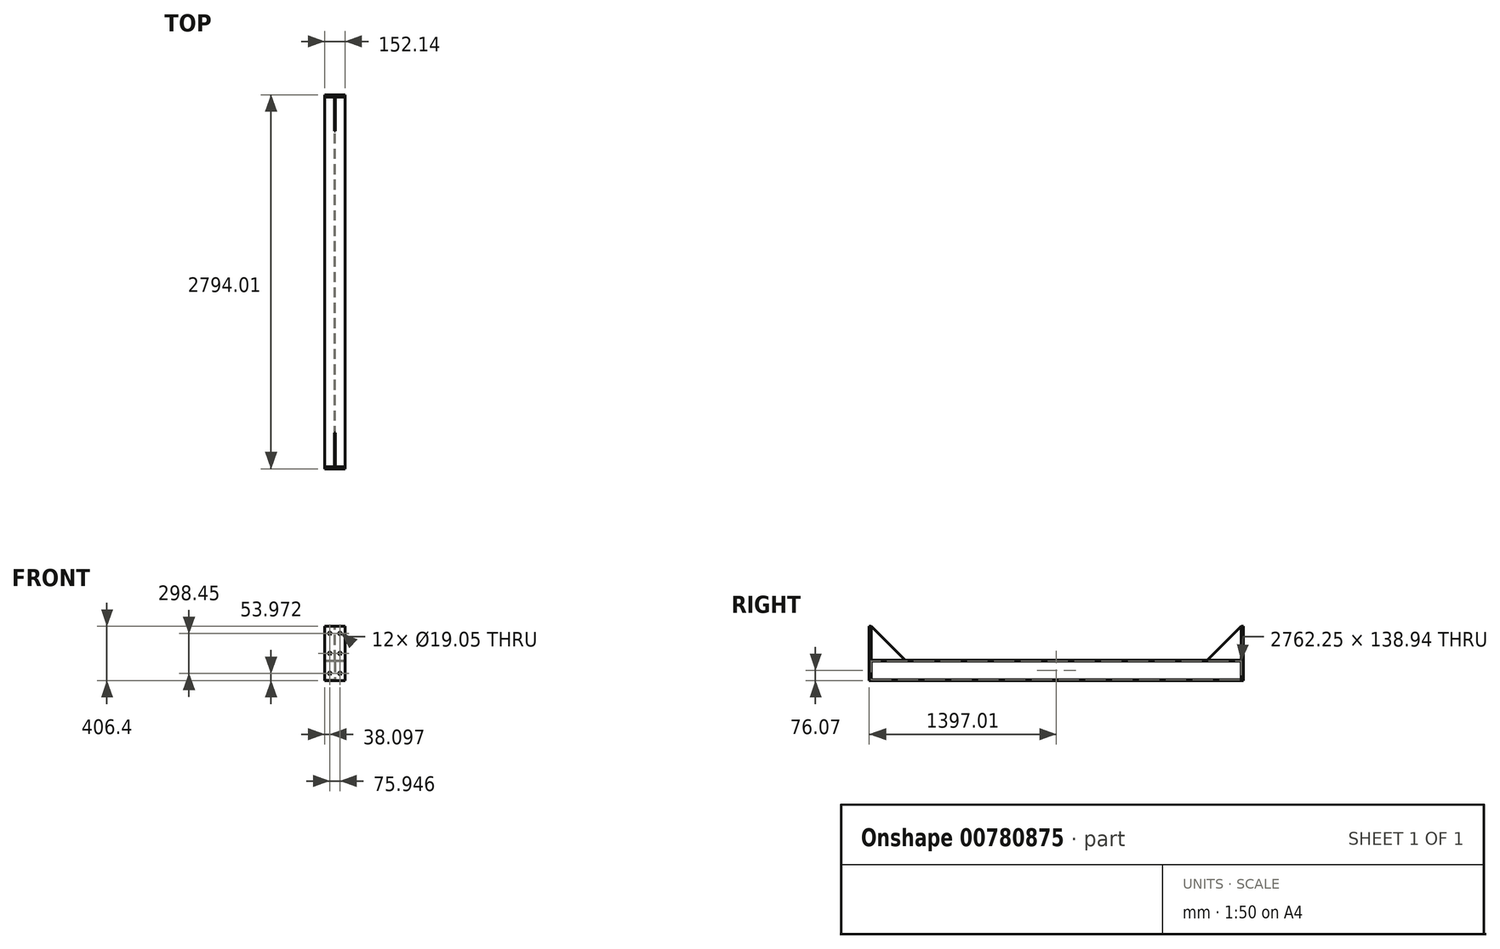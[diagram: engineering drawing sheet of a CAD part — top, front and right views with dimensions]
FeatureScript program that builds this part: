
annotation { "Feature Type Name" : "Feature", "Feature Type Description" : "" }
export const myFeature = defineFeature(function(context is Context, id is Id, definition is map)
    precondition{}
    {
        {
            var Q0;
            Q0=qCreatedBy(makeId("Front.planeOp"),FACE);
            var sketch = newSketch(context, id + "F0", { "sketchPlane" : qUnion([Q0])});
            skLineSegment(sketch, "E0", {"start": v(0, -76.07) * mm, "end": v(0, 76.07) * mm, "construction": true});
            skLineSegment(sketch, "E1", {"start": v(-76.07, 76.07) * mm, "end": v(76.07, 76.07) * mm});
            skLineSegment(sketch, "E2", {"start": v(-76.07, -76.07) * mm, "end": v(76.07, -76.07) * mm});
            skLineSegment(sketch, "E3", {"start": v(-76.07, 76.07) * mm, "end": v(-76.07, 69.47) * mm});
            skLineSegment(sketch, "E4", {"start": v(-76.07, 69.47) * mm, "end": v(-9.27, 69.47) * mm});
            skLineSegment(sketch, "E5", {"start": v(-2.92, 63.12) * mm, "end": v(-2.92, -63.12) * mm});
            skLineSegment(sketch, "E6", {"start": v(-9.27, -69.47) * mm, "end": v(-76.07, -69.47) * mm});
            skLineSegment(sketch, "E7", {"start": v(-76.07, -69.47) * mm, "end": v(-76.07, -76.07) * mm});
            skLineSegment(sketch, "E8", {"start": v(-2.92, 69.47) * mm, "end": v(2.92, 69.47) * mm, "construction": true});
            skLineSegment(sketch, "E9", {"start": v(9.27, 69.47) * mm, "end": v(76.07, 69.47) * mm});
            skLineSegment(sketch, "E10", {"start": v(76.07, 69.47) * mm, "end": v(76.07, 76.07) * mm});
            skLineSegment(sketch, "E11", {"start": v(-2.92, -69.47) * mm, "end": v(2.92, -69.47) * mm, "construction": true});
            skLineSegment(sketch, "E12", {"start": v(2.92, 63.12) * mm, "end": v(2.92, -63.12) * mm});
            skLineSegment(sketch, "E13", {"start": v(9.27, -69.47) * mm, "end": v(76.07, -69.47) * mm});
            skLineSegment(sketch, "E14", {"start": v(76.07, -69.47) * mm, "end": v(76.07, -76.07) * mm});
            skLineSegment(sketch, "E15", {"start": v(0, 69.47) * mm, "end": v(0, -69.47) * mm, "construction": true});
            skPoint(sketch, "E16.visualSharp", {"position": v(2.92, 69.47) * mm});
            skArc(sketch, "E16.filletArc", {"start": v(9.27, 69.47) * mm, "mid": v(4.78, 67.6) * mm, "end": v(2.92, 63.12) * mm});
            skPoint(sketch, "E17.visualSharp", {"position": v(-2.92, 69.47) * mm});
            skArc(sketch, "E17.filletArc", {"start": v(-2.92, 63.12) * mm, "mid": v(-4.78, 67.6) * mm, "end": v(-9.27, 69.47) * mm});
            skPoint(sketch, "E18.visualSharp", {"position": v(-2.92, -69.47) * mm});
            skArc(sketch, "E18.filletArc", {"start": v(-9.27, -69.47) * mm, "mid": v(-4.78, -67.6) * mm, "end": v(-2.92, -63.12) * mm});
            skPoint(sketch, "E19.visualSharp", {"position": v(2.92, -69.47) * mm});
            skArc(sketch, "E19.filletArc", {"start": v(2.92, -63.12) * mm, "mid": v(4.78, -67.6) * mm, "end": v(9.27, -69.47) * mm});
            skSolve(sketch);
        }
        {
            var Q0;
            Q0=makeQuery(id+"F0.imprint","IMPRINT",FACE,{"disambiguationData":[TD([[makeQuery(id+"F0.imprint","IMPRINT",EDGE,{"derivedFrom":sQuery(id+"F0.wireOp",EDGE,"E1")}),-1.0]])]});
            extrude(context, id + "F1", {"entities" : qUnion([Q0]), "depth" : 2762.25 * mm, "offsetDistance" : 25.4 * mm});
        }
        {
            var Q0;
            Q0=makeQuery(id+"F1.opExtrude","CAP_FACE",FACE,{"disambiguationData":[OSD([sQuery(id+"F0.wireOp",EDGE,"E1"),sQuery(id+"F0.wireOp",EDGE,"E2"),sQuery(id+"F0.wireOp",EDGE,"E3"),sQuery(id+"F0.wireOp",EDGE,"E4"),sQuery(id+"F0.wireOp",EDGE,"E5"),sQuery(id+"F0.wireOp",EDGE,"E6"),sQuery(id+"F0.wireOp",EDGE,"E7"),sQuery(id+"F0.wireOp",EDGE,"E9"),sQuery(id+"F0.wireOp",EDGE,"E10"),sQuery(id+"F0.wireOp",EDGE,"E12"),sQuery(id+"F0.wireOp",EDGE,"E13"),sQuery(id+"F0.wireOp",EDGE,"E14"),sQuery(id+"F0.wireOp",EDGE,"E16.filletArc"),sQuery(id+"F0.wireOp",EDGE,"E17.filletArc"),sQuery(id+"F0.wireOp",EDGE,"E18.filletArc"),sQuery(id+"F0.wireOp",EDGE,"E19.filletArc")])],"isStart":false});
            var sketch = newSketch(context, id + "F2", { "sketchPlane" : qUnion([Q0])});
            skLineSegment(sketch, "E20.0", {"start": v(-76.07, -76.07) * mm, "end": v(76.07, -76.07) * mm});
            skLineSegment(sketch, "E21", {"start": v(-76.07, -76.07) * mm, "end": v(-76.07, 330.33) * mm});
            skLineSegment(sketch, "E22", {"start": v(76.07, -76.07) * mm, "end": v(76.07, 330.33) * mm});
            skLineSegment(sketch, "E23", {"start": v(76.07, 330.33) * mm, "end": v(-76.07, 330.33) * mm});
            skSolve(sketch);
        }
        {
            var Q0;
            {var subQ2=makeQuery(id+"F1.opExtrude","CAP_EDGE",EDGE,{"disambiguationData":[OSD([sQuery(id+"F0.wireOp",EDGE,"E9")])],"isStart":false});Q0=makeQuery(id+"F2.imprint","IMPRINT",FACE,{"disambiguationData":[TD([[makeQuery(id+"F2.imprint","IMPRINT",EDGE,{"derivedFrom":subQ2}),-1.0]])]});}
            var Q1;
            {var subQ2=makeQuery(id+"F1.opExtrude","CAP_EDGE",EDGE,{"disambiguationData":[OSD([sQuery(id+"F0.wireOp",EDGE,"E4")])],"isStart":false});Q1=makeQuery(id+"F2.imprint","IMPRINT",FACE,{"disambiguationData":[TD([[makeQuery(id+"F2.imprint","IMPRINT",EDGE,{"derivedFrom":subQ2}),-1.0]])]});}
            var Q2;
            {var subQ2=sQuery(id+"F2.wireOp",EDGE,"E23");Q2=makeQuery(id+"F2.imprint","IMPRINT",FACE,{"disambiguationData":[TD([[makeQuery(id+"F2.imprint","IMPRINT",EDGE,{"derivedFrom":subQ2}),1.0]])]});}
            var Q3;
            {var subQ4=sQuery(id+"F2.wireOp",EDGE,"E20.0");Q3=makeQuery(id+"F2.imprint","IMPRINT",FACE,{"disambiguationData":[TD([[makeQuery(id+"F2.imprint","IMPRINT",EDGE,{"derivedFrom":subQ4}),1.0]])]});}
            extrude(context, id + "F3", {"entities" : qUnion([Q0, Q1, Q2, Q3]), "operationType" : NewBodyOperationType.ADD, "depth" : 15.88 * mm, "offsetDistance" : 25.4 * mm});
        }
        {
            var Q0;
            Q0=makeQuery(id+"F1.opExtrude","CAP_FACE",FACE,{"disambiguationData":[OSD([sQuery(id+"F0.wireOp",EDGE,"E1"),sQuery(id+"F0.wireOp",EDGE,"E2"),sQuery(id+"F0.wireOp",EDGE,"E3"),sQuery(id+"F0.wireOp",EDGE,"E4"),sQuery(id+"F0.wireOp",EDGE,"E5"),sQuery(id+"F0.wireOp",EDGE,"E6"),sQuery(id+"F0.wireOp",EDGE,"E7"),sQuery(id+"F0.wireOp",EDGE,"E9"),sQuery(id+"F0.wireOp",EDGE,"E10"),sQuery(id+"F0.wireOp",EDGE,"E12"),sQuery(id+"F0.wireOp",EDGE,"E13"),sQuery(id+"F0.wireOp",EDGE,"E14"),sQuery(id+"F0.wireOp",EDGE,"E16.filletArc"),sQuery(id+"F0.wireOp",EDGE,"E17.filletArc"),sQuery(id+"F0.wireOp",EDGE,"E18.filletArc"),sQuery(id+"F0.wireOp",EDGE,"E19.filletArc")])],"isStart":true});
            var sketch = newSketch(context, id + "F4", { "sketchPlane" : qUnion([Q0])});
            skLineSegment(sketch, "E24.0", {"start": v(76.07, -76.07) * mm, "end": v(-76.07, -76.07) * mm});
            skLineSegment(sketch, "E25", {"start": v(-76.07, -76.07) * mm, "end": v(-76.07, 330.33) * mm});
            skLineSegment(sketch, "E26", {"start": v(-76.07, 330.33) * mm, "end": v(76.07, 330.33) * mm});
            skLineSegment(sketch, "E27", {"start": v(76.07, 330.33) * mm, "end": v(76.07, -76.07) * mm});
            skSolve(sketch);
        }
        {
            var Q0;
            {var subQ2=sQuery(id+"F4.wireOp",EDGE,"E26");Q0=makeQuery(id+"F4.imprint","IMPRINT",FACE,{"disambiguationData":[TD([[makeQuery(id+"F4.imprint","IMPRINT",EDGE,{"derivedFrom":subQ2}),-1.0]])]});}
            var Q1;
            {var subQ3=sQuery(id+"F4.wireOp",EDGE,"E24.0");Q1=makeQuery(id+"F4.imprint","IMPRINT",FACE,{"disambiguationData":[TD([[makeQuery(id+"F4.imprint","IMPRINT",EDGE,{"derivedFrom":subQ3}),-1.0]])]});}
            var Q2;
            {var subQ1=makeQuery(id+"F1.opExtrude","CAP_EDGE",EDGE,{"disambiguationData":[OSD([sQuery(id+"F0.wireOp",EDGE,"E4")])],"isStart":true});Q2=makeQuery(id+"F4.imprint","IMPRINT",FACE,{"disambiguationData":[TD([[makeQuery(id+"F4.imprint","IMPRINT",EDGE,{"derivedFrom":subQ1}),1.0]])]});}
            var Q3;
            {var subQ0=makeQuery(id+"F1.opExtrude","CAP_EDGE",EDGE,{"disambiguationData":[OSD([sQuery(id+"F0.wireOp",EDGE,"E9")])],"isStart":true});Q3=makeQuery(id+"F4.imprint","IMPRINT",FACE,{"disambiguationData":[TD([[makeQuery(id+"F4.imprint","IMPRINT",EDGE,{"derivedFrom":subQ0}),1.0]])]});}
            extrude(context, id + "F5", {"entities" : qUnion([Q0, Q1, Q2, Q3]), "operationType" : NewBodyOperationType.ADD, "depth" : 15.88 * mm, "offsetDistance" : 25.4 * mm});
        }
        {
            var Q0;
            Q0=qCreatedBy(makeId("Right.planeOp"),FACE);
            var sketch = newSketch(context, id + "F6", { "sketchPlane" : qUnion([Q0])});
            skLineSegment(sketch, "E28.0", {"start": v(0, 330.07) * mm, "end": v(0, 76.07) * mm});
            skLineSegment(sketch, "E29", {"start": v(0, 76.07) * mm, "end": v(-254, 76.07) * mm});
            skLineSegment(sketch, "E30", {"start": v(-254, 76.07) * mm, "end": v(0, 330.07) * mm});
            skPoint(sketch, "E31.orphan", {"position": v(0, 330.33) * mm});
            skLineSegment(sketch, "E32.0", {"start": v(-2762.25, 76.07) * mm, "end": v(-2762.25, 330.07) * mm});
            skLineSegment(sketch, "E33.0", {"start": v(-2762.25, 76.07) * mm, "end": v(-2508.25, 76.07) * mm});
            skLineSegment(sketch, "E34", {"start": v(-2508.25, 76.07) * mm, "end": v(-2762.25, 330.07) * mm});
            skLineSegment(sketch, "E35.trimOffspring", {"start": v(-254, 76.07) * mm, "end": v(0, 76.07) * mm});
            skPoint(sketch, "E36.orphan", {"position": v(-2762.25, 330.33) * mm});
            skSolve(sketch);
        }
        {
            var Q0;
            Q0=makeQuery(id+"F6.imprint","IMPRINT",FACE,{"disambiguationData":[TD([[makeQuery(id+"F6.imprint","IMPRINT",EDGE,{"derivedFrom":sQuery(id+"F6.wireOp",EDGE,"E28.0")}),-1.0]])]});
            var Q1;
            Q1=makeQuery(id+"F6.imprint","IMPRINT",FACE,{"disambiguationData":[TD([[makeQuery(id+"F6.imprint","IMPRINT",EDGE,{"derivedFrom":sQuery(id+"F6.wireOp",EDGE,"E32.0")}),-1.0]])]});
            extrude(context, id + "F7", {"entities" : qUnion([Q0, Q1]), "operationType" : NewBodyOperationType.ADD, "endBound" : BoundingType.SYMMETRIC, "depth" : 6.35 * mm, "offsetDistance" : 25.4 * mm});
        }
        {
            var Q0;
            Q0=makeQuery(id+"F5.opExtrude","CAP_FACE",FACE,{"disambiguationData":[OSD([sQuery(id+"F4.wireOp",EDGE,"E24.0"),sQuery(id+"F4.wireOp",EDGE,"E25"),sQuery(id+"F4.wireOp",EDGE,"E26"),sQuery(id+"F4.wireOp",EDGE,"E27")])],"isStart":false});
            var sketch = newSketch(context, id + "F8", { "sketchPlane" : qUnion([Q0])});
            skLineSegment(sketch, "E37", {"start": v(-37.97, 330.33) * mm, "end": v(-37.97, -76.07) * mm, "construction": true});
            skLineSegment(sketch, "E38", {"start": v(37.97, 330.33) * mm, "end": v(37.97, -76.07) * mm, "construction": true});
            skLineSegment(sketch, "E39", {"start": v(-76.07, 276.35) * mm, "end": v(76.07, 276.35) * mm, "construction": true});
            skLineSegment(sketch, "E40", {"start": v(-76.07, 127.13) * mm, "end": v(76.07, 127.13) * mm, "construction": true});
            skLineSegment(sketch, "E41", {"start": v(-76.07, -22.1) * mm, "end": v(76.07, -22.1) * mm, "construction": true});
            skCircle(sketch, "E42", {"center": v(-37.97, 276.35) * mm, "radius": 9.53 * mm});
            skCircle(sketch, "E43", {"center": v(37.97, 276.35) * mm, "radius": 9.53 * mm});
            skCircle(sketch, "E44", {"center": v(-37.97, 127.13) * mm, "radius": 9.53 * mm});
            skCircle(sketch, "E45", {"center": v(37.97, 127.13) * mm, "radius": 9.53 * mm});
            skCircle(sketch, "E46", {"center": v(-37.97, -22.1) * mm, "radius": 9.53 * mm});
            skCircle(sketch, "E47", {"center": v(37.97, -22.1) * mm, "radius": 9.53 * mm});
            skSolve(sketch);
        }
        {
            var Q0;
            Q0=makeQuery(id+"F8.imprint","IMPRINT",FACE,{"disambiguationData":[TD([[makeQuery(id+"F8.imprint","IMPRINT",EDGE,{"derivedFrom":sQuery(id+"F8.wireOp",EDGE,"E42")}),1.0]])]});
            var Q1;
            Q1=makeQuery(id+"F8.imprint","IMPRINT",FACE,{"disambiguationData":[TD([[makeQuery(id+"F8.imprint","IMPRINT",EDGE,{"derivedFrom":sQuery(id+"F8.wireOp",EDGE,"E45")}),1.0]])]});
            var Q2;
            Q2=makeQuery(id+"F8.imprint","IMPRINT",FACE,{"disambiguationData":[TD([[makeQuery(id+"F8.imprint","IMPRINT",EDGE,{"derivedFrom":sQuery(id+"F8.wireOp",EDGE,"E44")}),1.0]])]});
            var Q3;
            Q3=makeQuery(id+"F8.imprint","IMPRINT",FACE,{"disambiguationData":[TD([[makeQuery(id+"F8.imprint","IMPRINT",EDGE,{"derivedFrom":sQuery(id+"F8.wireOp",EDGE,"E46")}),1.0]])]});
            var Q4;
            Q4=makeQuery(id+"F8.imprint","IMPRINT",FACE,{"disambiguationData":[TD([[makeQuery(id+"F8.imprint","IMPRINT",EDGE,{"derivedFrom":sQuery(id+"F8.wireOp",EDGE,"E47")}),1.0]])]});
            var Q5;
            Q5=makeQuery(id+"F8.imprint","IMPRINT",FACE,{"disambiguationData":[TD([[makeQuery(id+"F8.imprint","IMPRINT",EDGE,{"derivedFrom":sQuery(id+"F8.wireOp",EDGE,"E43")}),1.0]])]});
            extrude(context, id + "F9", {"entities" : qUnion([Q0, Q1, Q2, Q3, Q4, Q5]), "operationType" : NewBodyOperationType.REMOVE, "oppositeDirection" : true, "depth" : 2794 * mm, "offsetDistance" : 25.4 * mm});
        }
    });
